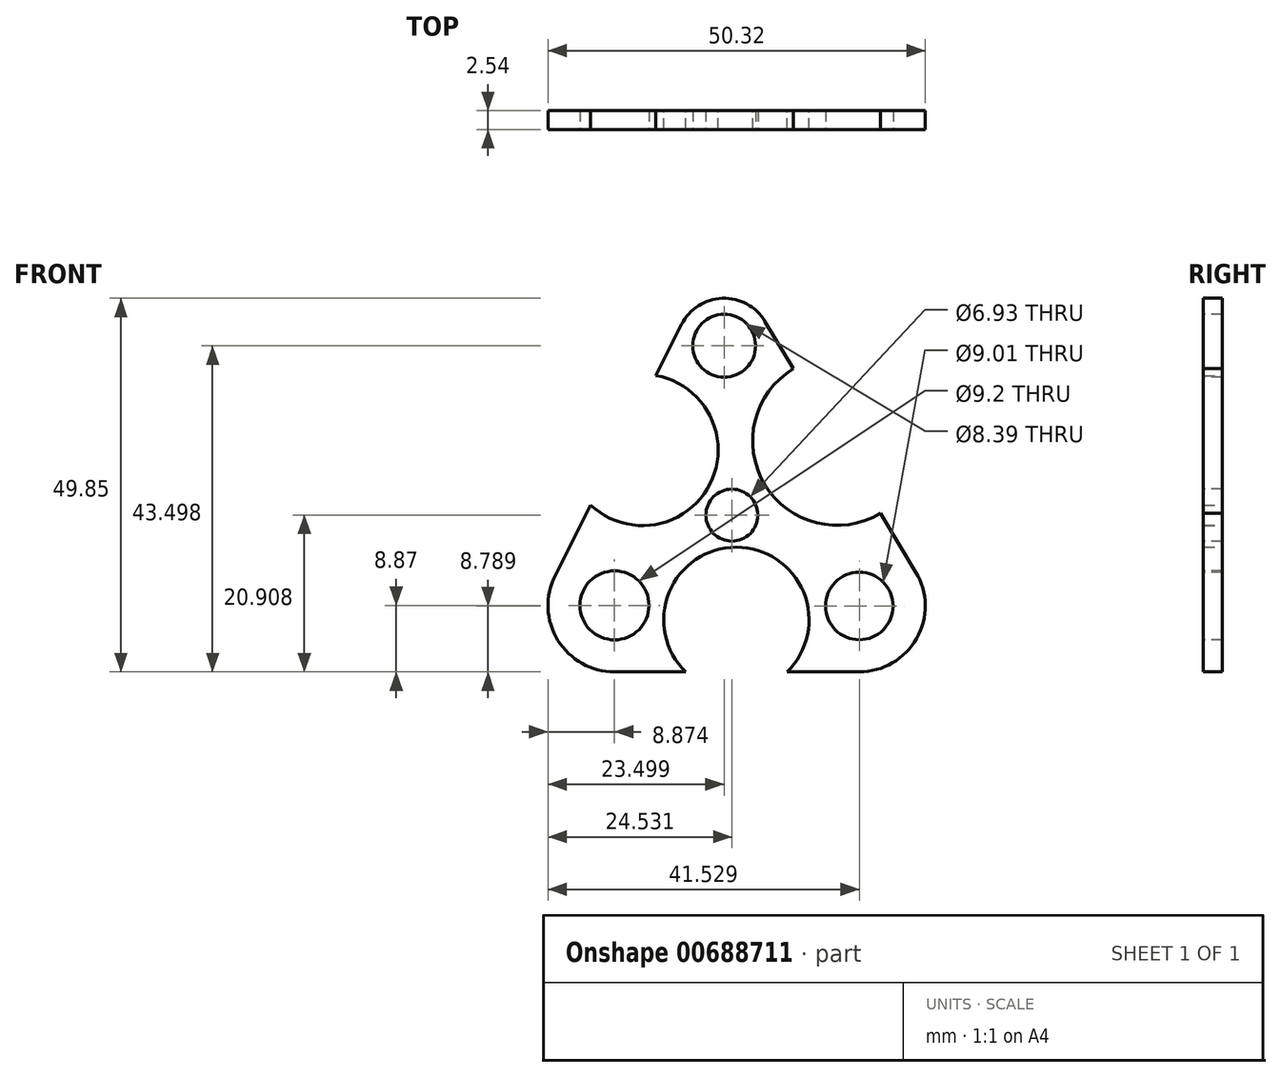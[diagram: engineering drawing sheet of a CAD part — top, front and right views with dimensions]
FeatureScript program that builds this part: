
annotation { "Feature Type Name" : "Feature", "Feature Type Description" : "" }
export const myFeature = defineFeature(function(context is Context, id is Id, definition is map)
    precondition{}
    {
        {
            var Q0;
            Q0=qCreatedBy(makeId("Front.planeOp"),FACE);
            var sketch = newSketch(context, id + "F0", { "sketchPlane" : qUnion([Q0])});
            skLineSegment(sketch, "E0", {"start": v(-8, 13.32) * mm, "end": v(-28.13, 46.77) * mm});
            skLineSegment(sketch, "E1", {"start": v(-39.24, 46.36) * mm, "end": v(-56.12, 12.86) * mm});
            skLineSegment(sketch, "E2", {"start": v(-48.2, 0) * mm, "end": v(-15.54, 0) * mm});
            skPoint(sketch, "E3.visualSharp", {"position": v(-34.06, 56.64) * mm});
            skArc(sketch, "E3.filletArc", {"start": v(-28.13, 46.77) * mm, "mid": v(-33.8, 49.84) * mm, "end": v(-39.24, 46.36) * mm});
            skPoint(sketch, "E4.visualSharp", {"position": v(-62.6, 0) * mm});
            skArc(sketch, "E4.filletArc", {"start": v(-56.12, 12.86) * mm, "mid": v(-55.75, 4.22) * mm, "end": v(-48.2, 0) * mm});
            skPoint(sketch, "E5.visualSharp", {"position": v(0, 0) * mm});
            skArc(sketch, "E5.filletArc", {"start": v(-15.54, 0) * mm, "mid": v(-7.9, 4.46) * mm, "end": v(-8, 13.32) * mm});
            skArc(sketch, "E6", {"start": v(-51.38, 22.26) * mm, "mid": v(-35.45, 25.07) * mm, "end": v(-42.67, 39.54) * mm});
            skPoint(sketch, "E7", {"position": v(-47.68, 29.6) * mm});
            skArc(sketch, "E8", {"start": v(-24.32, 40.44) * mm, "mid": v(-28.16, 25) * mm, "end": v(-12.72, 21.16) * mm});
            skArc(sketch, "E9", {"start": v(-25.18, 0) * mm, "mid": v(-31.95, 16.63) * mm, "end": v(-38.7, 0) * mm});
            skSolve(sketch);
        }
        {
            var Q0;
            {var subQ2=sQuery(id+"F0.wireOp",EDGE,"E3.filletArc");Q0=makeQuery(id+"F0.imprint","IMPRINT",FACE,{"disambiguationData":[TD([[makeQuery(id+"F0.imprint","IMPRINT",EDGE,{"derivedFrom":subQ2}),1.0]])]});}
            extrude(context, id + "F1", {"entities" : qUnion([Q0]), "depth" : 2.54 * mm, "offsetDistance" : 25.4 * mm});
        }
        {
            var Q0;
            Q0=makeQuery(id+"F1.opExtrude","CAP_FACE",FACE,{"disambiguationData":[OSD([sQuery(id+"F0.wireOp",EDGE,"E0"),sQuery(id+"F0.wireOp",EDGE,"E1"),sQuery(id+"F0.wireOp",EDGE,"E2"),sQuery(id+"F0.wireOp",EDGE,"E3.filletArc"),sQuery(id+"F0.wireOp",EDGE,"E4.filletArc"),sQuery(id+"F0.wireOp",EDGE,"E5.filletArc"),sQuery(id+"F0.wireOp",EDGE,"E6"),sQuery(id+"F0.wireOp",EDGE,"E8"),sQuery(id+"F0.wireOp",EDGE,"E9")])],"isStart":false});
            var sketch = newSketch(context, id + "F2", { "sketchPlane" : qUnion([Q0])});
            skCircle(sketch, "E10", {"center": v(-32.54, 20.9) * mm, "radius": 3.47 * mm});
            skSolve(sketch);
        }
        {
            var Q0;
            Q0=makeQuery(id+"F2.imprint","IMPRINT",FACE,{"disambiguationData":[TD([[makeQuery(id+"F2.imprint","IMPRINT",EDGE,{"derivedFrom":sQuery(id+"F2.wireOp",EDGE,"E10")}),1.0]])]});
            extrude(context, id + "F3", {"entities" : qUnion([Q0]), "operationType" : NewBodyOperationType.REMOVE, "oppositeDirection" : true, "depth" : 25.4 * mm, "offsetDistance" : 25.4 * mm});
        }
        {
            var Q0;
            Q0=makeQuery(id+"F1.opExtrude","CAP_FACE",FACE,{"disambiguationData":[OSD([sQuery(id+"F0.wireOp",EDGE,"E0"),sQuery(id+"F0.wireOp",EDGE,"E1"),sQuery(id+"F0.wireOp",EDGE,"E2"),sQuery(id+"F0.wireOp",EDGE,"E3.filletArc"),sQuery(id+"F0.wireOp",EDGE,"E4.filletArc"),sQuery(id+"F0.wireOp",EDGE,"E5.filletArc"),sQuery(id+"F0.wireOp",EDGE,"E6"),sQuery(id+"F0.wireOp",EDGE,"E8"),sQuery(id+"F0.wireOp",EDGE,"E9")])],"isStart":false});
            var sketch = newSketch(context, id + "F4", { "sketchPlane" : qUnion([Q0])});
            skCircle(sketch, "E11", {"center": v(-48.2, 8.87) * mm, "radius": 4.6 * mm});
            skCircle(sketch, "E12", {"center": v(-15.54, 8.79) * mm, "radius": 4.5 * mm});
            skSolve(sketch);
        }
        {
            var Q0;
            Q0=makeQuery(id+"F4.imprint","IMPRINT",FACE,{"disambiguationData":[TD([[makeQuery(id+"F4.imprint","IMPRINT",EDGE,{"derivedFrom":sQuery(id+"F4.wireOp",EDGE,"E11")}),1.0]])]});
            var Q1;
            Q1=makeQuery(id+"F4.imprint","IMPRINT",FACE,{"disambiguationData":[TD([[makeQuery(id+"F4.imprint","IMPRINT",EDGE,{"derivedFrom":sQuery(id+"F4.wireOp",EDGE,"E12")}),1.0]])]});
            extrude(context, id + "F5", {"entities" : qUnion([Q0, Q1]), "operationType" : NewBodyOperationType.REMOVE, "oppositeDirection" : true, "depth" : 25.4 * mm, "offsetDistance" : 25.4 * mm});
        }
        {
            var Q0;
            Q0=makeQuery(id+"F1.opExtrude","CAP_FACE",FACE,{"disambiguationData":[OSD([sQuery(id+"F0.wireOp",EDGE,"E0"),sQuery(id+"F0.wireOp",EDGE,"E1"),sQuery(id+"F0.wireOp",EDGE,"E2"),sQuery(id+"F0.wireOp",EDGE,"E3.filletArc"),sQuery(id+"F0.wireOp",EDGE,"E4.filletArc"),sQuery(id+"F0.wireOp",EDGE,"E5.filletArc"),sQuery(id+"F0.wireOp",EDGE,"E6"),sQuery(id+"F0.wireOp",EDGE,"E8"),sQuery(id+"F0.wireOp",EDGE,"E9")])],"isStart":false});
            var sketch = newSketch(context, id + "F6", { "sketchPlane" : qUnion([Q0])});
            skCircle(sketch, "E13", {"center": v(-33.57, 43.5) * mm, "radius": 4.2 * mm});
            skSolve(sketch);
        }
        {
            var Q0;
            Q0=makeQuery(id+"F6.imprint","IMPRINT",FACE,{"disambiguationData":[TD([[makeQuery(id+"F6.imprint","IMPRINT",EDGE,{"derivedFrom":sQuery(id+"F6.wireOp",EDGE,"E13")}),1.0]])]});
            extrude(context, id + "F7", {"entities" : qUnion([Q0]), "operationType" : NewBodyOperationType.REMOVE, "oppositeDirection" : true, "depth" : 25.4 * mm, "offsetDistance" : 25.4 * mm});
        }
    });
